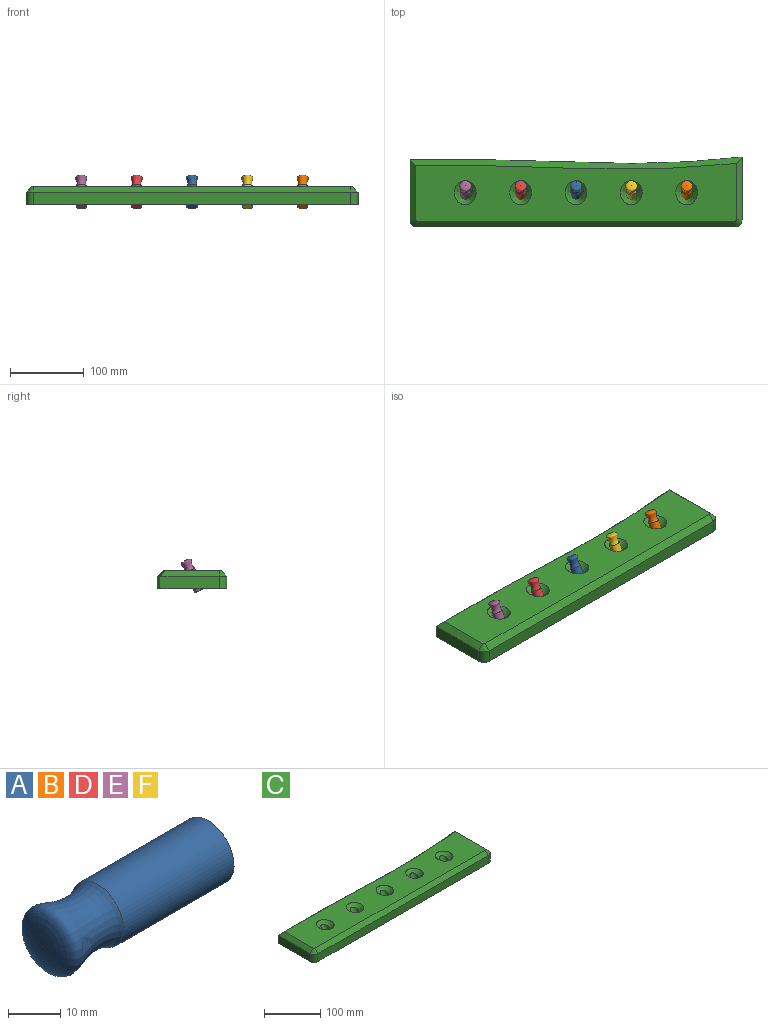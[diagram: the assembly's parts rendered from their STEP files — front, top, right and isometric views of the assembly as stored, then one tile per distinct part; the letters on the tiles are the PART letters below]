
ASSEMBLY  parts=6 mates=1
PART A: 3 faces, bbox 45x15x15 mm
  f0: revolved ~15.02x15.02mm, area 742.3mm2, adj f2
  f1: plane 14x14mm, normal (1,0,0), area 153.9mm2, adj f2
  f2: cylinder r=7mm len=30mm, axis (-1,0,0), area 1319.5mm2, adj f0,f1
PART B: same geometry as A
PART C: 24 faces, bbox 501.3x103x37.7 mm
  f0: plane 80.85x17.15mm, normal (-1,0,0), area 1386.7mm2, adj f4,f10,f11,f14
  f1: plane 430x17.15mm, normal (0,-1,0), area 7375.2mm2, adj f4,f11,f12,f15
  f2: plane 84.73x17.15mm, normal (1,0,0), area 1453.3mm2, adj f4,f10,f12,f18
  f3: plane 439.71x83.49mm, normal (0,0,1), area 27984.6mm2, adj f13,f14,f15,f16,f17,f18,f19,f20
  f4: plane 455.06x97.26mm, normal (0,0,-1), area 39204.8mm2, adj f0,f1,f2,f5,f6,f7,f8,f9
  f5: cylinder r=7mm len=32.34mm, axis (0,0.42,0.91), area 833.8mm2, adj f4,f23
  f6: cylinder r=7mm len=32.34mm, axis (0,0.42,0.91), area 833.8mm2, adj f4,f22
  f7: cylinder r=7mm len=32.34mm, axis (0,0.42,0.91), area 833.8mm2, adj f4,f21
  f8: cylinder r=7mm len=32.34mm, axis (0,0.42,0.91), area 833.8mm2, adj f4,f20
  f9: cylinder r=7mm len=32.34mm, axis (0,0.42,0.91), area 833.8mm2, adj f4,f19
  f10: extruded ~450x17.15mm, area 7725.5mm2, adj f0,f2,f4,f16
  f11: cylinder r=10mm len=17.15mm, axis (0,0,-1), area 269.4mm2, adj f0,f1,f4,f13
  f12: cylinder r=10mm len=17.15mm, axis (0,0,1), area 269.4mm2, adj f1,f2,f4,f17
  f13: cone r=2.15mm half-angle=45deg, axis (0,0,-1), area 105.9mm2, adj f3,f11,f14,f15
  f14: plane 80.86x7.86mm, normal (-0.71,0,0.71), area 854.9mm2, adj f0,f3,f13,f16
  f15: plane 430x7.85mm, normal (0,-0.71,0.71), area 4772.7mm2, adj f1,f3,f13,f17
  f16: bspline ~495.92x19.51mm, area 4912.2mm2, adj f3,f10,f14,f18
  f17: cone r=2.15mm half-angle=45deg, axis (0,0,-1), area 105.9mm2, adj f3,f12,f15,f18
  f18: plane 84.79x7.91mm, normal (0.71,0,0.71), area 891.5mm2, adj f2,f3,f16,f17
  f19: bspline ~32.77x29.7mm, area 823.3mm2, adj f3,f9
  f20: bspline ~32.77x29.7mm, area 823.3mm2, adj f3,f8
  f21: bspline ~32.77x29.7mm, area 823.3mm2, adj f3,f7
  f22: bspline ~32.77x29.7mm, area 823.3mm2, adj f3,f6
  f23: bspline ~32.77x29.7mm, area 823.3mm2, adj f3,f5
PART D: same geometry as A
PART E: same geometry as A
PART F: same geometry as A
PLACE A rot(axis=(-0.21,0.95,-0.21),92.7deg) t=(0,-6.21,38.5)mm
PLACE B rot(axis=(-0.21,0.95,-0.21),92.7deg) t=(150,-6.21,38.5)mm
PLACE C at identity
PLACE D rot(axis=(-0.21,0.95,-0.21),92.7deg) t=(-75,-6.21,38.5)mm
PLACE E rot(axis=(-0.21,0.95,-0.21),92.7deg) t=(-150,-6.21,38.5)mm
PLACE F rot(axis=(-0.21,0.95,-0.21),92.7deg) t=(75,-6.21,38.5)mm
MATE slider B.f2 <-> C.f9  axis (0,0.42,0.91) through (150,-25.22,-2.29)mm
